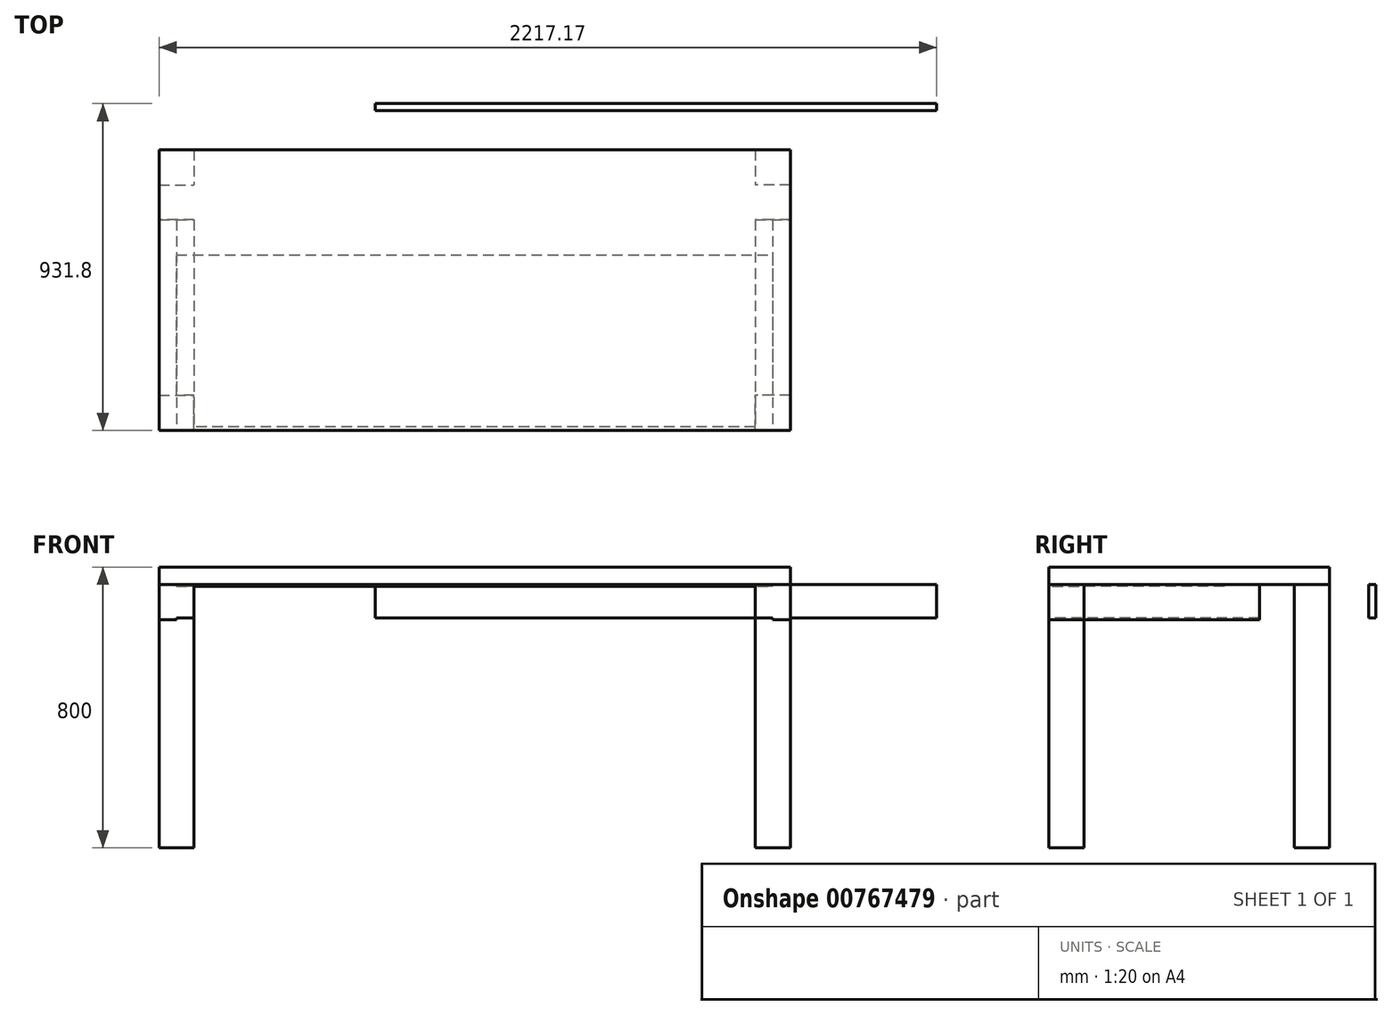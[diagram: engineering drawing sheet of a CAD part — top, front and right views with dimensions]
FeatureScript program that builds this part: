
annotation { "Feature Type Name" : "Feature", "Feature Type Description" : "" }
export const myFeature = defineFeature(function(context is Context, id is Id, definition is map)
    precondition{}
    {
        {
            var Q0;
            Q0=qCreatedBy(makeId("Top.planeOp"),FACE);
            var sketch = newSketch(context, id + "F0", { "sketchPlane" : qUnion([Q0])});
            skLineSegment(sketch, "E0.bottom", {"start": v(0, 800) * mm, "end": v(1800, 800) * mm});
            skLineSegment(sketch, "E0.top", {"start": v(0, 0) * mm, "end": v(1800, 0) * mm});
            skLineSegment(sketch, "E0.left", {"start": v(0, 800) * mm, "end": v(0, 0) * mm});
            skLineSegment(sketch, "E0.right", {"start": v(1800, 800) * mm, "end": v(1800, 0) * mm});
            skSolve(sketch);
        }
        {
            var Q0;
            Q0=makeQuery(id+"F0.imprint","IMPRINT",FACE,{"disambiguationData":[TD([[makeQuery(id+"F0.imprint","IMPRINT",EDGE,{"derivedFrom":sQuery(id+"F0.wireOp",EDGE,"E0.bottom")}),-1.0]])]});
            extrude(context, id + "F1", {"entities" : qUnion([Q0]), "depth" : 50 * mm, "offsetDistance" : 25 * mm});
        }
        {
            var Q0;
            Q0=qCreatedBy(makeId("Top.planeOp"),FACE);
            var sketch = newSketch(context, id + "F2", { "sketchPlane" : qUnion([Q0])});
            skLineSegment(sketch, "E1.bottom", {"start": v(0, 0) * mm, "end": v(100, 0) * mm});
            skLineSegment(sketch, "E1.top", {"start": v(0, 100) * mm, "end": v(100, 100) * mm});
            skLineSegment(sketch, "E1.left", {"start": v(0, 0) * mm, "end": v(0, 100) * mm});
            skLineSegment(sketch, "E1.right", {"start": v(100, 0) * mm, "end": v(100, 100) * mm});
            skLineSegment(sketch, "E2.MirrorCS", {"start": v(100, 800) * mm, "end": v(100, 700) * mm});
            skLineSegment(sketch, "E3.MirrorCS", {"start": v(0, 800) * mm, "end": v(0, 700) * mm});
            skLineSegment(sketch, "E4.MirrorCS", {"start": v(0, 800) * mm, "end": v(100, 800) * mm});
            skLineSegment(sketch, "E5.MirrorCS", {"start": v(0, 700) * mm, "end": v(100, 700) * mm});
            skLineSegment(sketch, "E6.MirrorCS", {"start": v(1700, 800) * mm, "end": v(1700, 700) * mm});
            skLineSegment(sketch, "E7.MirrorCS", {"start": v(1800, 800) * mm, "end": v(1800, 700) * mm});
            skLineSegment(sketch, "E8.MirrorCS", {"start": v(1800, 700) * mm, "end": v(1700, 700) * mm});
            skLineSegment(sketch, "E9.MirrorCS", {"start": v(1800, 800) * mm, "end": v(1700, 800) * mm});
            skLineSegment(sketch, "E10.MirrorCS", {"start": v(1700, 0) * mm, "end": v(1700, 100) * mm});
            skLineSegment(sketch, "E11.MirrorCS", {"start": v(1800, 0) * mm, "end": v(1800, 100) * mm});
            skLineSegment(sketch, "E12.MirrorCS", {"start": v(1800, 0) * mm, "end": v(1700, 0) * mm});
            skLineSegment(sketch, "E13.MirrorCS", {"start": v(1800, 100) * mm, "end": v(1700, 100) * mm});
            skSolve(sketch);
        }
        {
            var Q0;
            Q0=makeQuery(id+"F2.imprint","IMPRINT",FACE,{"disambiguationData":[TD([[makeQuery(id+"F2.imprint","IMPRINT",EDGE,{"derivedFrom":sQuery(id+"F2.wireOp",EDGE,"E1.bottom")}),1.0]])]});
            var Q1;
            Q1=makeQuery(id+"F2.imprint","IMPRINT",FACE,{"disambiguationData":[TD([[makeQuery(id+"F2.imprint","IMPRINT",EDGE,{"derivedFrom":sQuery(id+"F2.wireOp",EDGE,"E10.MirrorCS")}),-1.0]])]});
            var Q2;
            Q2=makeQuery(id+"F2.imprint","IMPRINT",FACE,{"disambiguationData":[TD([[makeQuery(id+"F2.imprint","IMPRINT",EDGE,{"derivedFrom":sQuery(id+"F2.wireOp",EDGE,"E6.MirrorCS")}),1.0]])]});
            var Q3;
            Q3=makeQuery(id+"F2.imprint","IMPRINT",FACE,{"disambiguationData":[TD([[makeQuery(id+"F2.imprint","IMPRINT",EDGE,{"derivedFrom":sQuery(id+"F2.wireOp",EDGE,"E2.MirrorCS")}),-1.0]])]});
            extrude(context, id + "F3", {"entities" : qUnion([Q0, Q1, Q2, Q3]), "oppositeDirection" : true, "depth" : 750 * mm, "offsetDistance" : 25 * mm});
        }
        {
            var Q0;
            Q0=qCreatedBy(makeId("Front.planeOp"),FACE);
            var sketch = newSketch(context, id + "F4", { "sketchPlane" : qUnion([Q0])});
            skLineSegment(sketch, "E14", {"start": v(0, 0) * mm, "end": v(0, -100) * mm});
            skLineSegment(sketch, "E15", {"start": v(0, -100) * mm, "end": v(50, -100) * mm});
            skLineSegment(sketch, "E16", {"start": v(50, -100) * mm, "end": v(50, -95) * mm});
            skLineSegment(sketch, "E17", {"start": v(50, -95) * mm, "end": v(100, -95) * mm});
            skLineSegment(sketch, "E18", {"start": v(100, -95) * mm, "end": v(100, 0) * mm});
            skLineSegment(sketch, "E19", {"start": v(100, 0) * mm, "end": v(0, 0) * mm});
            skLineSegment(sketch, "E20.MirrorCS", {"start": v(1750, -100) * mm, "end": v(1750, -95) * mm});
            skLineSegment(sketch, "E21.MirrorCS", {"start": v(1800, 0) * mm, "end": v(1800, -100) * mm});
            skLineSegment(sketch, "E22.MirrorCS", {"start": v(1800, -100) * mm, "end": v(1750, -100) * mm});
            skLineSegment(sketch, "E23.MirrorCS", {"start": v(1700, 0) * mm, "end": v(1800, 0) * mm});
            skLineSegment(sketch, "E24.MirrorCS", {"start": v(1750, -95) * mm, "end": v(1700, -95) * mm});
            skLineSegment(sketch, "E25.MirrorCS", {"start": v(1700, -95) * mm, "end": v(1700, 0) * mm});
            skSolve(sketch);
        }
        {
            var Q0;
            Q0=makeQuery(id+"F4.imprint","IMPRINT",FACE,{"disambiguationData":[TD([[makeQuery(id+"F4.imprint","IMPRINT",EDGE,{"derivedFrom":sQuery(id+"F4.wireOp",EDGE,"E14")}),1.0]])]});
            var Q1;
            Q1=makeQuery(id+"F4.imprint","IMPRINT",FACE,{"disambiguationData":[TD([[makeQuery(id+"F4.imprint","IMPRINT",EDGE,{"derivedFrom":sQuery(id+"F4.wireOp",EDGE,"E20.MirrorCS")}),-1.0]])]});
            extrude(context, id + "F5", {"entities" : qUnion([Q0, Q1]), "oppositeDirection" : true, "depth" : 600 * mm, "offsetDistance" : 25 * mm});
        }
        {
            var Q0;
            Q0=qCreatedBy(makeId("Top.planeOp"),FACE);
            var sketch = newSketch(context, id + "F6", { "sketchPlane" : qUnion([Q0])});
            skLineSegment(sketch, "E26", {"start": v(100, 10) * mm, "end": v(100, 100) * mm});
            skLineSegment(sketch, "E27", {"start": v(100, 100) * mm, "end": v(50, 100) * mm});
            skLineSegment(sketch, "E28", {"start": v(50, 100) * mm, "end": v(50, 500) * mm});
            skLineSegment(sketch, "E29", {"start": v(50, 500) * mm, "end": v(1750, 500) * mm});
            skLineSegment(sketch, "E30", {"start": v(1750, 500) * mm, "end": v(1750, 100) * mm});
            skLineSegment(sketch, "E31", {"start": v(1750, 100) * mm, "end": v(1700, 100) * mm});
            skLineSegment(sketch, "E32", {"start": v(1700, 100) * mm, "end": v(1700, 10) * mm});
            skLineSegment(sketch, "E33", {"start": v(1700, 10) * mm, "end": v(100, 10) * mm});
            skSolve(sketch);
        }
        {
            var Q0;
            Q0=makeQuery(id+"F6.imprint","IMPRINT",FACE,{"disambiguationData":[TD([[makeQuery(id+"F6.imprint","IMPRINT",EDGE,{"derivedFrom":sQuery(id+"F6.wireOp",EDGE,"E26")}),-1.0]])]});
            extrude(context, id + "F7", {"entities" : qUnion([Q0]), "oppositeDirection" : true, "depth" : 5 * mm, "offsetDistance" : 25 * mm});
        }
        {
            var Q0;
            Q0=qCreatedBy(makeId("Top.planeOp"),FACE);
            var sketch = newSketch(context, id + "F8", { "sketchPlane" : qUnion([Q0])});
            skLineSegment(sketch, "E34.bottom", {"start": v(617.17, 931.8) * mm, "end": v(2217.17, 931.8) * mm});
            skLineSegment(sketch, "E34.top", {"start": v(617.17, 911.8) * mm, "end": v(2217.17, 911.8) * mm});
            skLineSegment(sketch, "E34.left", {"start": v(617.17, 931.8) * mm, "end": v(617.17, 911.8) * mm});
            skLineSegment(sketch, "E34.right", {"start": v(2217.17, 931.8) * mm, "end": v(2217.17, 911.8) * mm});
            skSolve(sketch);
        }
        {
            var Q0;
            Q0=makeQuery(id+"F8.imprint","IMPRINT",FACE,{"disambiguationData":[TD([[makeQuery(id+"F8.imprint","IMPRINT",EDGE,{"derivedFrom":sQuery(id+"F8.wireOp",EDGE,"E34.bottom")}),-1.0]])]});
            extrude(context, id + "F9", {"entities" : qUnion([Q0]), "oppositeDirection" : true, "depth" : 95 * mm, "offsetDistance" : 25 * mm});
        }
    });
